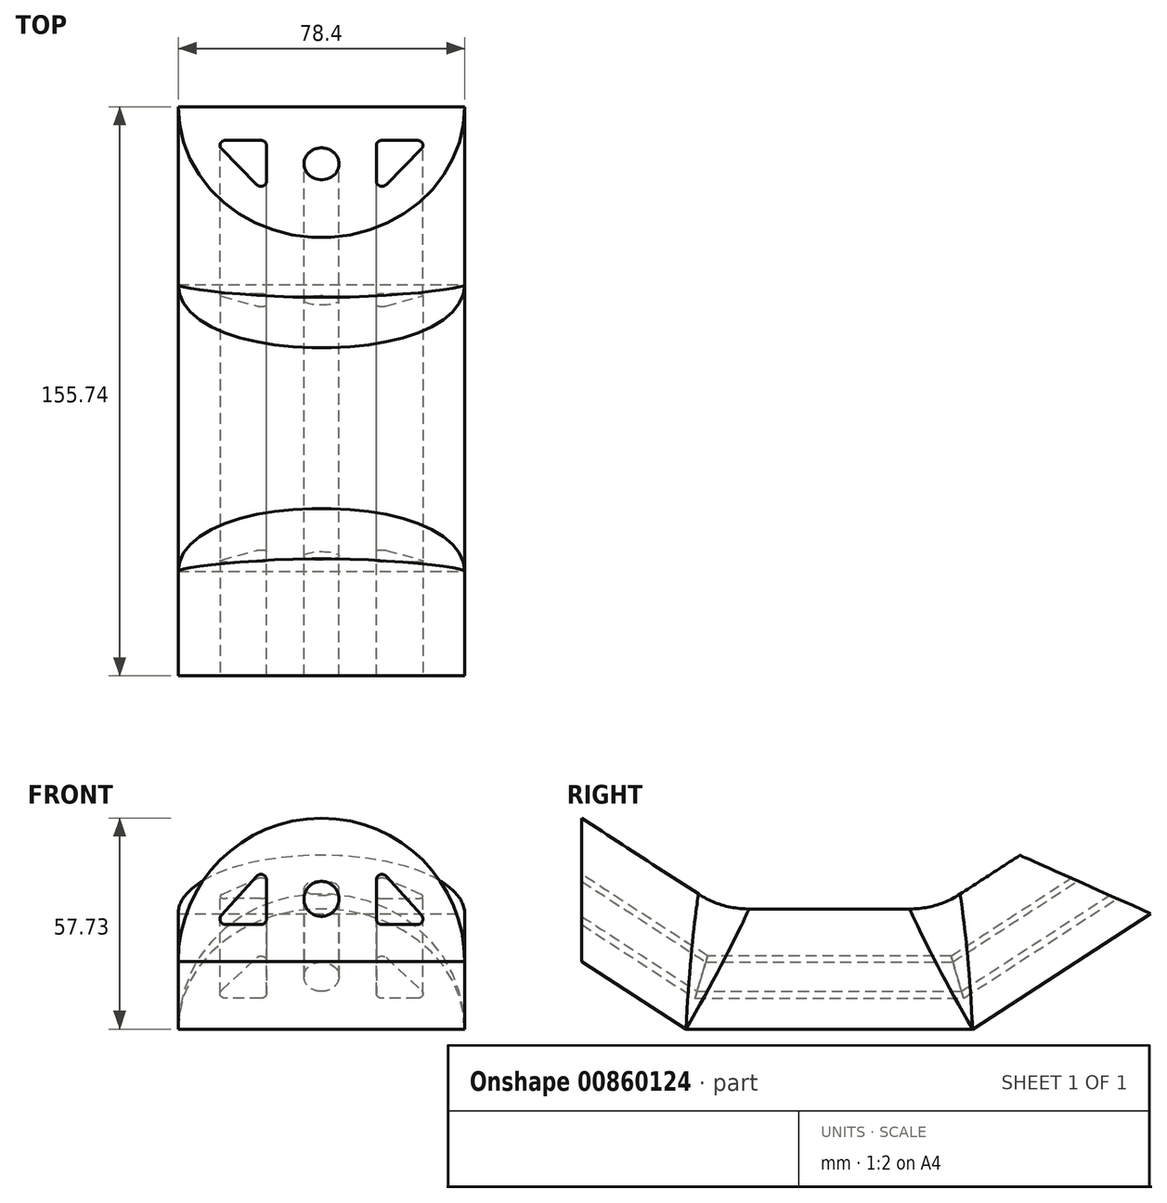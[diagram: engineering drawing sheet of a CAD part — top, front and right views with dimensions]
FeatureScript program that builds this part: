
annotation { "Feature Type Name" : "Feature", "Feature Type Description" : "" }
export const myFeature = defineFeature(function(context is Context, id is Id, definition is map)
    precondition{}
    {
        {
            var Q0;
            Q0=qCreatedBy(makeId("Front.planeOp"),FACE);
            var sketch = newSketch(context, id + "F0", { "sketchPlane" : qUnion([Q0])});
            skArc(sketch, "E0", {"start": v(39.2, 0) * mm, "mid": v(0, 39.2) * mm, "end": v(-39.2, 0) * mm});
            skLineSegment(sketch, "E1", {"start": v(-39.2, 0) * mm, "end": v(39.2, 0) * mm});
            skCircle(sketch, "E2", {"center": v(0, 17.11) * mm, "radius": 4.79 * mm});
            skLineSegment(sketch, "E3", {"start": v(-15.03, 22.32) * mm, "end": v(-15.03, 11.6) * mm});
            skLineSegment(sketch, "E4", {"start": v(-16.56, 10.07) * mm, "end": v(-26.25, 10.07) * mm});
            skLineSegment(sketch, "E5", {"start": v(-27.38, 12.61) * mm, "end": v(-17.69, 23.34) * mm});
            skLineSegment(sketch, "E6.MirrorCS", {"start": v(15.03, 22.32) * mm, "end": v(15.03, 11.6) * mm});
            skLineSegment(sketch, "E7.MirrorCS", {"start": v(27.38, 12.61) * mm, "end": v(17.69, 23.34) * mm});
            skLineSegment(sketch, "E8.MirrorCS", {"start": v(16.56, 10.07) * mm, "end": v(26.25, 10.07) * mm});
            skPoint(sketch, "E9.visualSharp", {"position": v(-15.03, 26.28) * mm});
            skArc(sketch, "E9.filletArc", {"start": v(-15.03, 22.32) * mm, "mid": v(-16.01, 23.74) * mm, "end": v(-17.69, 23.34) * mm});
            skPoint(sketch, "E10.visualSharp", {"position": v(-29.68, 10.07) * mm});
            skArc(sketch, "E10.filletArc", {"start": v(-27.38, 12.61) * mm, "mid": v(-27.64, 10.97) * mm, "end": v(-26.25, 10.07) * mm});
            skPoint(sketch, "E11.visualSharp", {"position": v(-15.03, 10.07) * mm});
            skArc(sketch, "E11.filletArc", {"start": v(-16.56, 10.07) * mm, "mid": v(-15.48, 10.51) * mm, "end": v(-15.03, 11.6) * mm});
            skPoint(sketch, "E12.visualSharp", {"position": v(15.03, 26.28) * mm});
            skArc(sketch, "E12.filletArc", {"start": v(17.69, 23.34) * mm, "mid": v(16.01, 23.74) * mm, "end": v(15.03, 22.32) * mm});
            skPoint(sketch, "E13.visualSharp", {"position": v(15.03, 10.07) * mm});
            skArc(sketch, "E13.filletArc", {"start": v(15.03, 11.6) * mm, "mid": v(15.48, 10.51) * mm, "end": v(16.56, 10.07) * mm});
            skPoint(sketch, "E14.visualSharp", {"position": v(29.68, 10.07) * mm});
            skArc(sketch, "E14.filletArc", {"start": v(26.25, 10.07) * mm, "mid": v(27.64, 10.97) * mm, "end": v(27.38, 12.61) * mm});
            skSolve(sketch);
        }
        {
            var Q0;
            Q0=qCreatedBy(makeId("Right.planeOp"),FACE);
            var sketch = newSketch(context, id + "F1", { "sketchPlane" : qUnion([Q0])});
            skLineSegment(sketch, "E15", {"start": v(0, 22.1) * mm, "end": v(34.03, 0) * mm});
            skLineSegment(sketch, "E16", {"start": v(34.03, 0) * mm, "end": v(101.52, 0) * mm});
            skLineSegment(sketch, "E17", {"start": v(101.52, 0) * mm, "end": v(135.56, 22.1) * mm});
            skPoint(sketch, "E18.visualSharp", {"position": v(34.03, 0) * mm});
            skLineSegment(sketch, "E18.filletArc", {"start": v(34.03, 0) * mm, "end": v(34.03, 0) * mm});
            skPoint(sketch, "E19.visualSharp", {"position": v(101.52, 0) * mm});
            skLineSegment(sketch, "E19.filletArc", {"start": v(101.52, 0) * mm, "end": v(101.52, 0) * mm});
            skSolve(sketch);
        }
        {
            var Q0;
            Q0=makeQuery(id+"F0.imprint","IMPRINT",FACE,{"disambiguationData":[TD([[makeQuery(id+"F0.imprint","IMPRINT",EDGE,{"derivedFrom":sQuery(id+"F0.wireOp",EDGE,"E0")}),1.0]])]});
            var Q1;
            Q1=sQuery(id+"F0.wireOp",EDGE,"E0");
            var Q2;
            Q2=sQuery(id+"F0.wireOp",EDGE,"E1");
            var Q3;
            Q3=sQuery(id+"F0.wireOp",EDGE,"E3");
            var Q4;
            Q4=sQuery(id+"F0.wireOp",EDGE,"E9.filletArc");
            var Q5;
            Q5=sQuery(id+"F0.wireOp",EDGE,"E5");
            var Q6;
            Q6=sQuery(id+"F0.wireOp",EDGE,"E4");
            var Q7;
            Q7=sQuery(id+"F0.wireOp",EDGE,"E10.filletArc");
            var Q8;
            Q8=sQuery(id+"F0.wireOp",EDGE,"E11.filletArc");
            var Q9;
            Q9=sQuery(id+"F0.wireOp",EDGE,"E2");
            var Q10;
            Q10=sQuery(id+"F0.wireOp",EDGE,"E6.MirrorCS");
            var Q11;
            Q11=sQuery(id+"F0.wireOp",EDGE,"E12.filletArc");
            var Q12;
            Q12=sQuery(id+"F0.wireOp",EDGE,"E7.MirrorCS");
            var Q13;
            Q13=sQuery(id+"F0.wireOp",EDGE,"E14.filletArc");
            var Q14;
            Q14=sQuery(id+"F0.wireOp",EDGE,"E8.MirrorCS");
            var Q15;
            Q15=sQuery(id+"F0.wireOp",EDGE,"E13.filletArc");
            var Q16;
            Q16=sQuery(id+"F1.wireOp",EDGE,"E15");
            var Q17;
            Q17=sQuery(id+"F1.wireOp",EDGE,"E16");
            var Q18;
            Q18=sQuery(id+"F1.wireOp",EDGE,"E17");
            sweep(context, id + "F2", {"profiles" : qUnion([Q0]), "surfaceProfiles" : qUnion([Q1, Q2, Q3, Q4, Q5, Q6, Q7, Q8, Q9, Q10, Q11, Q12, Q13, Q14, Q15]), "path" : qUnion([Q16, Q17, Q18])});
        }
        {
            var Q0;
            Q0=makeQuery(id+"F2.opSweep","MID_CAP_EDGE",EDGE,{"disambiguationData":[OSD([sQuery(id+"F0.wireOp",EDGE,"E0"),sQuery(id+"F1.wireOp",VERTEX,"E16.start")])],"capPos":1.0});
            var Q1;
            Q1=makeQuery(id+"F2.opSweep","MID_CAP_EDGE",EDGE,{"disambiguationData":[OSD([sQuery(id+"F0.wireOp",EDGE,"E0"),sQuery(id+"F1.wireOp",VERTEX,"E17.start")])],"capPos":2.0});
            fillet(context, id + "F3", {"entities" : qUnion([Q0, Q1]), "radius" : 25.4 * mm, "tangentPropagation" : true, "allowEdgeOverflow" : false});
        }
    });
